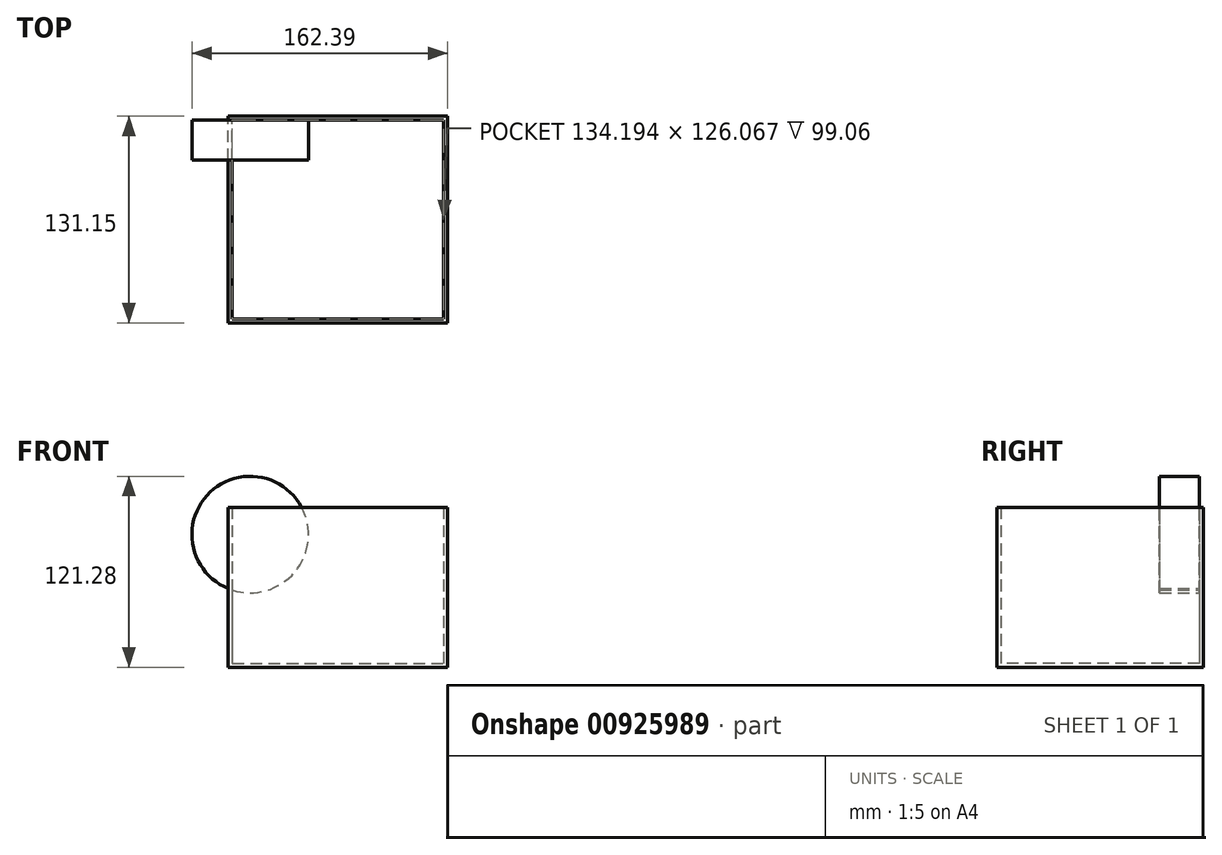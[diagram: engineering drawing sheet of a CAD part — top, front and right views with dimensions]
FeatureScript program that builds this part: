
annotation { "Feature Type Name" : "Feature", "Feature Type Description" : "" }
export const myFeature = defineFeature(function(context is Context, id is Id, definition is map)
    precondition{}
    {
        {
            var Q0;
            Q0=qCreatedBy(makeId("Top.planeOp"),FACE);
            var sketch = newSketch(context, id + "F0", { "sketchPlane" : qUnion([Q0])});
            skLineSegment(sketch, "E0.bottom", {"start": v(-72.31, 67.13) * mm, "end": v(66.96, 67.13) * mm});
            skLineSegment(sketch, "E0.top", {"start": v(-72.31, -64.02) * mm, "end": v(66.96, -64.02) * mm});
            skLineSegment(sketch, "E0.left", {"start": v(-72.31, 67.13) * mm, "end": v(-72.31, -64.02) * mm});
            skLineSegment(sketch, "E0.right", {"start": v(66.96, 67.13) * mm, "end": v(66.96, -64.02) * mm});
            skSolve(sketch);
        }
        {
            var Q0;
            Q0=makeQuery(id+"F0.imprint","IMPRINT",FACE,{"disambiguationData":[TD([[makeQuery(id+"F0.imprint","IMPRINT",EDGE,{"derivedFrom":sQuery(id+"F0.wireOp",EDGE,"E0.bottom")}),-1.0]])]});
            extrude(context, id + "F1", {"entities" : qUnion([Q0]), "depth" : 101.6 * mm, "offsetDistance" : 25.4 * mm});
        }
        {
            var Q0;
            Q0=makeQuery(id+"F1.opExtrude","CAP_FACE",FACE,{"disambiguationData":[OSD([sQuery(id+"F0.wireOp",EDGE,"E0.bottom"),sQuery(id+"F0.wireOp",EDGE,"E0.top"),sQuery(id+"F0.wireOp",EDGE,"E0.left"),sQuery(id+"F0.wireOp",EDGE,"E0.right")])],"isStart":false});
            shell(context, id + "F2", {"entities" : qUnion([Q0]), "thickness" : 2.54 * mm});
        }
        {
            var Q0;
            Q0=makeQuery(id+"F2.opShell","OFFSET_FACE",FACE,{"disambiguationData":[OSD([sQuery(id+"F0.wireOp",EDGE,"E0.bottom")])]});
            var sketch = newSketch(context, id + "F3", { "sketchPlane" : qUnion([Q0])});
            skCircle(sketch, "E1", {"center": v(-58.43, 84.27) * mm, "radius": 37 * mm});
            skSolve(sketch);
        }
        {
            var Q0;
            {var subQ0=sQuery(id+"F3.wireOp",EDGE,"E1");var subQ1=sQuery(id+"F0.wireOp",EDGE,"E0.bottom");var subQ4=makeQuery(id+"F2.opShell","OFFSET_EDGE",EDGE,{"disambiguationData":[OSD([subQ1]),TDD([makeQuery(id+"F1.opExtrude","CAP_EDGE",EDGE,{"disambiguationData":[OSD([subQ1])],"isStart":false})])]});var subQ5=makeQuery(id+"F3.imprint","INTERSECT",VERTEX,{"derivedFrom":[subQ4,subQ0]});Q0=makeQuery(id+"F3.imprint","IMPRINT",FACE,{"disambiguationData":[TD([[makeQuery(id+"F3.imprint","IMPRINT",EDGE,{"disambiguationData":[TD([[subQ5,-1.0]])],"derivedFrom":subQ0}),1.0]])]});}
            var Q1;
            {var subQ0=sQuery(id+"F3.wireOp",EDGE,"E1");var subQ1=sQuery(id+"F0.wireOp",EDGE,"E0.bottom");var subQ4=makeQuery(id+"F2.opShell","OFFSET_EDGE",EDGE,{"disambiguationData":[OSD([subQ1]),TDD([makeQuery(id+"F1.opExtrude","CAP_EDGE",EDGE,{"disambiguationData":[OSD([subQ1])],"isStart":false})])]});var subQ5=makeQuery(id+"F3.imprint","INTERSECT",VERTEX,{"derivedFrom":[subQ4,subQ0]});Q1=makeQuery(id+"F3.imprint","IMPRINT",FACE,{"disambiguationData":[TD([[makeQuery(id+"F3.imprint","IMPRINT",EDGE,{"disambiguationData":[TD([[subQ5,1.0]])],"derivedFrom":subQ0}),1.0]])]});}
            extrude(context, id + "F4", {"entities" : qUnion([Q0, Q1]), "operationType" : NewBodyOperationType.ADD, "depth" : 25.4 * mm, "offsetDistance" : 25.4 * mm});
        }
    });
